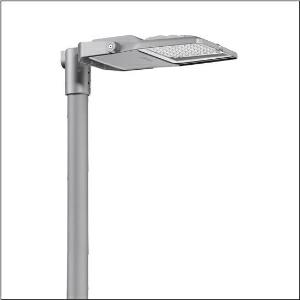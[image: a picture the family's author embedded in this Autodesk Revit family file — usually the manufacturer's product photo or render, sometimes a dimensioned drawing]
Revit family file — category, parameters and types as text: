
# Revit family: floodlight_fl_21_iq_mini___pl33t_5xa7771c4f3a_1d16
name_source: partatom
category: Lighting Fixtures
units: mm (PartAtom-declared; Revit-internal decimal feet)

## family parameters
Cut with Voids When Loaded = No
Host = Face
Light Source = No
Part Type = Normal
Room Calculation Point = No
Round Connector Dimension = Use Diameter
Shared = No

## types (1)
- --- (1 x LED, 12570 lm, 87.2 W, 4000K)
    Apparent Load = 87 VA
    CIE Flux Codes = 26 75 99 100 100
    Color Rendering = 70
    Color Temperature = 4000K
    Default Elevation = 1800 mm
    Description = Floodlight FL 21 iQ mini, floodlight, primary light control with lens, of PMMA, primary optical cover: protective disc, of toughened safety glass, transparent, light distribution: PL33T, light emission: direct distribution, installation type: surface-mounted, LED, High Power LED, rated luminous flux: 12.570lm, luminous efficacy: 144lm/W, light colour: 740, colour temperature: 4000K, control: Auto-Match, Temp-Guard, Lumen-Switch, Night-Set, Smart-Wire, Light-Fading, Desk-Remote (wireless, voltage-free reading and setting of iQ features in the workshop via application-optimized NFC function/RFID function), optimised constant luminous flux control (CLO 2.0), with terminal, 6-pole, mains connection: 220..240V, AC, 50/60Hz, start of lifetime: 87W, end of service life: 92W, reduction: 40W, luminaire housing, of diecast aluminium, powder-coated, Siteco® metallic grey (DB 702S), corrosivity category C5 mid according to DIN EN ISO 12944, sealing non-destructively replaceable, please order mast flange separately, mast bracket, of steel, galvanised, powder-coated, Siteco® metallic grey (DB 702S), protection rating (complete): IP66, insulation class (complete): insulation class II (safety insulation), certification: CE, ENEC, VDE, protection symbol: D, impact resistance: IK08, permissible operating ambient temperature: -40..+40°C, permissible operating ambient temperature for outdoor applications: -40..+50°C, standard: DIN EN 12944, LABS conformity tested according to VDMA 24364:2018-05, packaging unit: 1 piece

Light Distribution: PL33T
    Height = 70 mm
    Lamp = 1 x LED
    Lamp Light Flux = 12570 lm
    Lamp Power = 87.2 W
    Lamp count = 1
    Length = 485 mm
    Luminous efficacy = 144 lm/W
    Manufacturer = Siteco
    ModVariant = No
    Model = 5XA7771C4F3A
    Number of Poles = 1
    OnlyDefault = Yes
    Power Factor = 1
    Product Name = Floodlight FL 21 iQ mini | PL33T
    Product group = floodlight | pylon annexe
    ProductGroupID = 6200
    Protection Class = Protection class II
    Protection Degree = IP 66
    RLX_Detail_Level = 1
    RLX_Emergency_Light_Flux = 0 lm
    RLX_Emergency_Type = 0
    RLX_Emergency_Type_DB = No
    RlxData = <blob elided: 101289 chars, md5=03fe34f0>
    Socket = socket
    Standby Power = 0 W
    System Light Flux = 12570 lm
    System Power = 87 W
    Type Comments = factory setting: luminous flux: 100 % | dim-lin: 254 | 456 mA
    Type Image = l_1007125.jpg
    URL = http://relux.com
    VarID = @adj_119969
    Voltage = 0 V
    Weight = 0.00 kg
    Width = 337 mm

## geometry (parser evidence)
native form markers: Blend x4, Sweep x13
no freeform markers — native parametric forms only
